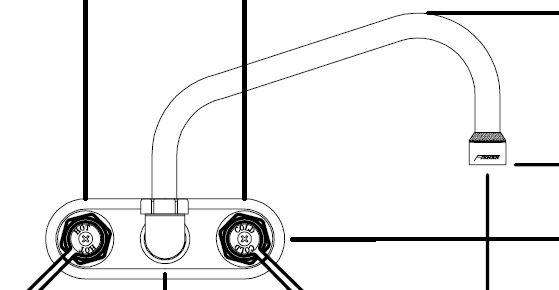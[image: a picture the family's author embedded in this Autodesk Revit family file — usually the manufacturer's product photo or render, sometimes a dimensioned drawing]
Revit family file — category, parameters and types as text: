
# Revit family: QF_FISHER_62448
name_source: partatom
category: Specialty Equipment
revit_build: Autodesk Revit 2015 (Build: 20140606_1530(x64)
units: mm (PartAtom-declared; Revit-internal decimal feet)

## types (1)
- QF_FISHER_62448
    A = 2 1/4"
    B = 5 7/8"
    C = 6"
    Cold Water Connection Height = 0"
    Cold Water Flow = 2 GPM
    Cold Water Maximum Pressure = 200.00 psi
    Cold Water Minimum Pressure = 80.00 psi
    Cold Water RI Height = 0"
    Cold Water Size = 1"
    Cold Water Temperature Recommended = 40 °F
    Depth = 8 3/8"
    Description = STAINLESS STEEL 4" C/C BACKSPLASH FAUCET
    Foodservice Equipment Identifier = Yes
    Height = 5 7/8"
    Hot Water Connection Height = 0"
    Hot Water Consumption = 0 GPM
    Hot Water Flow = 2 GPM
    Hot Water Maximum Pressure = 200.00 psi
    Hot Water Minimum Pressure = 80.00 psi
    Hot Water RI Height = 0"
    Hot Water Size = 1"
    Hot Water Temperature = 140 °F
    Identify Quantity as Lot = Yes
    Length = 4"
    Manufacturer = FISHER
    Model = 62448
    Weight in Pounds = 5

## geometry (parser evidence)
native form markers: Sweep x13
no freeform markers — native parametric forms only
